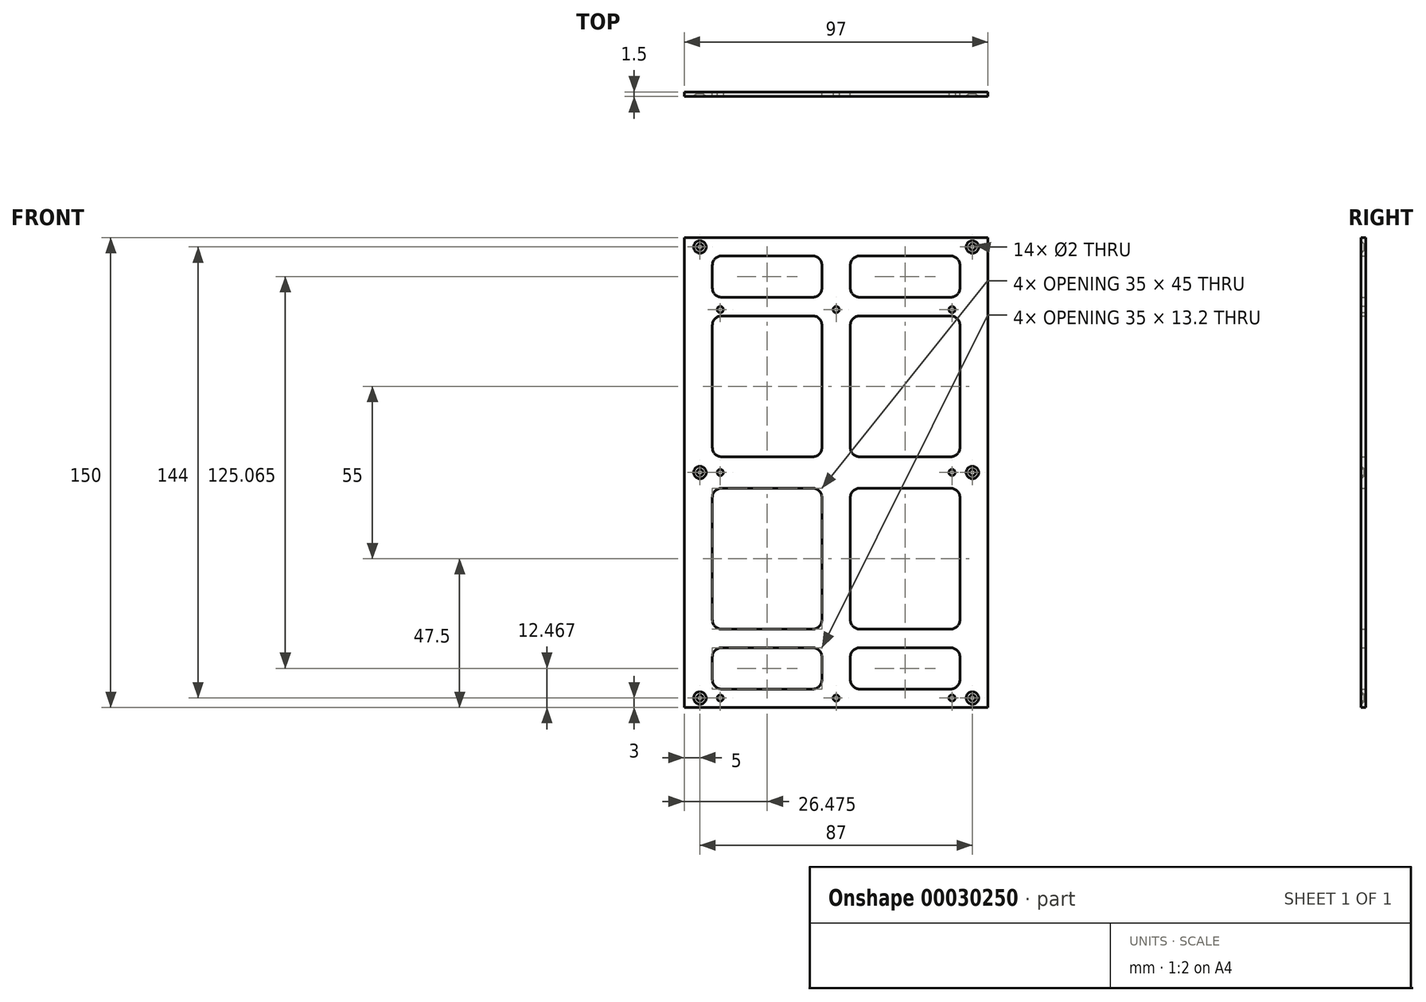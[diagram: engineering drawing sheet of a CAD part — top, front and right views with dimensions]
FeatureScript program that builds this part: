
annotation { "Feature Type Name" : "Feature", "Feature Type Description" : "" }
export const myFeature = defineFeature(function(context is Context, id is Id, definition is map)
    precondition{}
    {
        {
            var Q0;
            Q0=qCreatedBy(makeId("Front.planeOp"),FACE);
            var sketch = newSketch(context, id + "F0", { "sketchPlane" : qUnion([Q0])});
            skLineSegment(sketch, "E0.rect.bottom", {"start": v(-48.5, 75) * mm, "end": v(48.5, 75) * mm});
            skLineSegment(sketch, "E0.rect.top", {"start": v(-48.5, -75) * mm, "end": v(48.5, -75) * mm});
            skLineSegment(sketch, "E0.rect.left", {"start": v(-48.5, 75) * mm, "end": v(-48.5, -75) * mm});
            skLineSegment(sketch, "E0.rect.right", {"start": v(48.5, 75) * mm, "end": v(48.5, -75) * mm});
            skPoint(sketch, "E0.rect.middle", {"position": v(0, 0) * mm});
            skLineSegment(sketch, "E1.rect.bottom", {"start": v(-7.52, 5) * mm, "end": v(-36.52, 5) * mm});
            skLineSegment(sketch, "E1.rect.top", {"start": v(-7.52, 50) * mm, "end": v(-36.52, 50) * mm});
            skLineSegment(sketch, "E1.rect.left", {"start": v(-4.52, 8) * mm, "end": v(-4.52, 47) * mm});
            skLineSegment(sketch, "E1.rect.right", {"start": v(-39.52, 8) * mm, "end": v(-39.52, 47) * mm});
            skPoint(sketch, "E1.rect.middle", {"position": v(-22.02, 27.5) * mm});
            skPoint(sketch, "E2", {"position": v(0, 75) * mm});
            skPoint(sketch, "E3", {"position": v(-24.25, 75) * mm});
            skPoint(sketch, "E4.MirrorP", {"position": v(-24.25, -75) * mm});
            skPoint(sketch, "E5.visualSharp", {"position": v(-4.52, 5) * mm});
            skArc(sketch, "E5.filletArc", {"start": v(-7.52, 5) * mm, "mid": v(-5.4, 5.88) * mm, "end": v(-4.52, 8) * mm});
            skPoint(sketch, "E6.visualSharp", {"position": v(-4.52, 50) * mm});
            skArc(sketch, "E6.filletArc", {"start": v(-4.52, 47) * mm, "mid": v(-5.4, 49.12) * mm, "end": v(-7.52, 50) * mm});
            skPoint(sketch, "E7.visualSharp", {"position": v(-39.52, 50) * mm});
            skArc(sketch, "E7.filletArc", {"start": v(-36.52, 50) * mm, "mid": v(-38.65, 49.12) * mm, "end": v(-39.52, 47) * mm});
            skPoint(sketch, "E8.visualSharp", {"position": v(-39.52, 5) * mm});
            skArc(sketch, "E8.filletArc", {"start": v(-39.52, 8) * mm, "mid": v(-38.65, 5.88) * mm, "end": v(-36.52, 5) * mm});
            skLineSegment(sketch, "E9.MirrorCS", {"start": v(4.52, 8) * mm, "end": v(4.52, 47) * mm});
            skArc(sketch, "E10.MirrorCS", {"start": v(4.52, 47) * mm, "mid": v(5.4, 49.12) * mm, "end": v(7.52, 50) * mm});
            skLineSegment(sketch, "E11.MirrorCS", {"start": v(7.52, 50) * mm, "end": v(36.52, 50) * mm});
            skPoint(sketch, "E12.MirrorP", {"position": v(39.52, 50) * mm});
            skArc(sketch, "E13.MirrorCS", {"start": v(36.52, 50) * mm, "mid": v(38.65, 49.12) * mm, "end": v(39.52, 47) * mm});
            skLineSegment(sketch, "E14.MirrorCS", {"start": v(39.52, 8) * mm, "end": v(39.52, 47) * mm});
            skPoint(sketch, "E15.MirrorP", {"position": v(39.52, 5) * mm});
            skLineSegment(sketch, "E16.MirrorCS", {"start": v(7.52, 5) * mm, "end": v(36.52, 5) * mm});
            skArc(sketch, "E17.MirrorCS", {"start": v(39.52, 8) * mm, "mid": v(38.65, 5.88) * mm, "end": v(36.52, 5) * mm});
            skPoint(sketch, "E18.MirrorP", {"position": v(4.52, 5) * mm});
            skArc(sketch, "E19.MirrorCS", {"start": v(7.52, 5) * mm, "mid": v(5.4, 5.88) * mm, "end": v(4.52, 8) * mm});
            skPoint(sketch, "E20.MirrorP", {"position": v(4.52, 50) * mm});
            skArc(sketch, "E21.MirrorCS", {"start": v(36.52, -50) * mm, "mid": v(38.65, -49.12) * mm, "end": v(39.52, -47) * mm});
            skArc(sketch, "E22.MirrorCS", {"start": v(39.52, -8) * mm, "mid": v(38.65, -5.88) * mm, "end": v(36.52, -5) * mm});
            skArc(sketch, "E23.MirrorCS", {"start": v(7.52, -5) * mm, "mid": v(5.4, -5.88) * mm, "end": v(4.52, -8) * mm});
            skArc(sketch, "E24.MirrorCS", {"start": v(4.52, -47) * mm, "mid": v(5.4, -49.12) * mm, "end": v(7.52, -50) * mm});
            skPoint(sketch, "E25.MirrorP", {"position": v(39.52, -50) * mm});
            skLineSegment(sketch, "E26.MirrorCS", {"start": v(39.52, -8) * mm, "end": v(39.52, -47) * mm});
            skPoint(sketch, "E27.MirrorP", {"position": v(39.52, -5) * mm});
            skLineSegment(sketch, "E28.MirrorCS", {"start": v(4.52, -8) * mm, "end": v(4.52, -47) * mm});
            skPoint(sketch, "E29.MirrorP", {"position": v(4.52, -50) * mm});
            skLineSegment(sketch, "E30.MirrorCS", {"start": v(7.52, -5) * mm, "end": v(36.52, -5) * mm});
            skLineSegment(sketch, "E31.MirrorCS", {"start": v(7.52, -50) * mm, "end": v(36.52, -50) * mm});
            skPoint(sketch, "E32.MirrorP", {"position": v(4.52, -5) * mm});
            skArc(sketch, "E33.MirrorCS", {"start": v(-7.52, -5) * mm, "mid": v(-5.4, -5.88) * mm, "end": v(-4.52, -8) * mm});
            skArc(sketch, "E34.MirrorCS", {"start": v(-4.52, -47) * mm, "mid": v(-5.4, -49.12) * mm, "end": v(-7.52, -50) * mm});
            skArc(sketch, "E35.MirrorCS", {"start": v(-39.52, -8) * mm, "mid": v(-38.65, -5.88) * mm, "end": v(-36.52, -5) * mm});
            skArc(sketch, "E36.MirrorCS", {"start": v(-36.52, -50) * mm, "mid": v(-38.65, -49.12) * mm, "end": v(-39.52, -47) * mm});
            skPoint(sketch, "E37.MirrorP", {"position": v(-22.02, -27.5) * mm});
            skPoint(sketch, "E38.MirrorP", {"position": v(-4.52, -5) * mm});
            skPoint(sketch, "E39.MirrorP", {"position": v(-39.52, -50) * mm});
            skLineSegment(sketch, "E40.MirrorCS", {"start": v(-7.52, -5) * mm, "end": v(-36.52, -5) * mm});
            skLineSegment(sketch, "E41.MirrorCS", {"start": v(-7.52, -50) * mm, "end": v(-36.52, -50) * mm});
            skPoint(sketch, "E42.MirrorP", {"position": v(-4.52, -50) * mm});
            skLineSegment(sketch, "E43.MirrorCS", {"start": v(-4.52, -8) * mm, "end": v(-4.52, -47) * mm});
            skLineSegment(sketch, "E44.MirrorCS", {"start": v(-39.52, -8) * mm, "end": v(-39.52, -47) * mm});
            skPoint(sketch, "E45.MirrorP", {"position": v(-39.52, -5) * mm});
            skLineSegment(sketch, "E46.bottom", {"start": v(-7.52, 55.93) * mm, "end": v(-36.52, 55.93) * mm});
            skLineSegment(sketch, "E46.top", {"start": v(-7.52, 69.13) * mm, "end": v(-36.52, 69.13) * mm});
            skLineSegment(sketch, "E46.left", {"start": v(-4.52, 58.93) * mm, "end": v(-4.52, 66.13) * mm});
            skLineSegment(sketch, "E46.right", {"start": v(-39.52, 58.93) * mm, "end": v(-39.52, 66.13) * mm});
            skPoint(sketch, "E47.visualSharp", {"position": v(-39.52, 69.13) * mm});
            skArc(sketch, "E47.filletArc", {"start": v(-36.52, 69.13) * mm, "mid": v(-38.65, 68.26) * mm, "end": v(-39.52, 66.13) * mm});
            skPoint(sketch, "E48.visualSharp", {"position": v(-4.52, 69.13) * mm});
            skArc(sketch, "E48.filletArc", {"start": v(-4.52, 66.13) * mm, "mid": v(-5.4, 68.26) * mm, "end": v(-7.52, 69.13) * mm});
            skPoint(sketch, "E49.visualSharp", {"position": v(-4.52, 55.93) * mm});
            skArc(sketch, "E49.filletArc", {"start": v(-7.52, 55.93) * mm, "mid": v(-5.4, 56.8) * mm, "end": v(-4.52, 58.93) * mm});
            skPoint(sketch, "E50.visualSharp", {"position": v(-39.52, 55.93) * mm});
            skArc(sketch, "E50.filletArc", {"start": v(-39.52, 58.93) * mm, "mid": v(-38.65, 56.8) * mm, "end": v(-36.52, 55.93) * mm});
            skArc(sketch, "E51.MirrorCS", {"start": v(36.52, 69.13) * mm, "mid": v(38.65, 68.26) * mm, "end": v(39.52, 66.13) * mm});
            skArc(sketch, "E52.MirrorCS", {"start": v(4.52, 66.13) * mm, "mid": v(5.4, 68.26) * mm, "end": v(7.52, 69.13) * mm});
            skArc(sketch, "E53.MirrorCS", {"start": v(39.52, 58.93) * mm, "mid": v(38.65, 56.8) * mm, "end": v(36.52, 55.93) * mm});
            skArc(sketch, "E54.MirrorCS", {"start": v(7.52, 55.93) * mm, "mid": v(5.4, 56.8) * mm, "end": v(4.52, 58.93) * mm});
            skPoint(sketch, "E55.MirrorP", {"position": v(39.52, 55.93) * mm});
            skPoint(sketch, "E56.MirrorP", {"position": v(39.52, 69.13) * mm});
            skLineSegment(sketch, "E57.MirrorCS", {"start": v(39.52, 58.93) * mm, "end": v(39.52, 66.13) * mm});
            skPoint(sketch, "E58.MirrorP", {"position": v(4.52, 69.13) * mm});
            skLineSegment(sketch, "E59.MirrorCS", {"start": v(7.52, 69.13) * mm, "end": v(36.52, 69.13) * mm});
            skLineSegment(sketch, "E60.MirrorCS", {"start": v(4.52, 58.93) * mm, "end": v(4.52, 66.13) * mm});
            skLineSegment(sketch, "E61.MirrorCS", {"start": v(7.52, 55.93) * mm, "end": v(36.52, 55.93) * mm});
            skPoint(sketch, "E62.MirrorP", {"position": v(4.52, 55.93) * mm});
            skArc(sketch, "E63.MirrorCS", {"start": v(-4.52, -66.13) * mm, "mid": v(-5.4, -68.26) * mm, "end": v(-7.52, -69.13) * mm});
            skArc(sketch, "E64.MirrorCS", {"start": v(-36.52, -69.13) * mm, "mid": v(-38.65, -68.26) * mm, "end": v(-39.52, -66.13) * mm});
            skArc(sketch, "E65.MirrorCS", {"start": v(-39.52, -58.93) * mm, "mid": v(-38.65, -56.8) * mm, "end": v(-36.52, -55.93) * mm});
            skArc(sketch, "E66.MirrorCS", {"start": v(-7.52, -55.93) * mm, "mid": v(-5.4, -56.8) * mm, "end": v(-4.52, -58.93) * mm});
            skPoint(sketch, "E67.MirrorP", {"position": v(-39.52, -69.13) * mm});
            skPoint(sketch, "E68.MirrorP", {"position": v(-4.52, -55.93) * mm});
            skPoint(sketch, "E69.MirrorP", {"position": v(-4.52, -69.13) * mm});
            skLineSegment(sketch, "E70.MirrorCS", {"start": v(-39.52, -58.93) * mm, "end": v(-39.52, -66.13) * mm});
            skLineSegment(sketch, "E71.MirrorCS", {"start": v(-7.52, -69.13) * mm, "end": v(-36.52, -69.13) * mm});
            skPoint(sketch, "E72.MirrorP", {"position": v(-39.52, -55.93) * mm});
            skLineSegment(sketch, "E73.MirrorCS", {"start": v(-4.52, -58.93) * mm, "end": v(-4.52, -66.13) * mm});
            skLineSegment(sketch, "E74.MirrorCS", {"start": v(-7.52, -55.93) * mm, "end": v(-36.52, -55.93) * mm});
            skArc(sketch, "E75.MirrorCS", {"start": v(7.52, -55.93) * mm, "mid": v(5.4, -56.8) * mm, "end": v(4.52, -58.93) * mm});
            skArc(sketch, "E76.MirrorCS", {"start": v(39.52, -58.93) * mm, "mid": v(38.65, -56.8) * mm, "end": v(36.52, -55.93) * mm});
            skArc(sketch, "E77.MirrorCS", {"start": v(4.52, -66.13) * mm, "mid": v(5.4, -68.26) * mm, "end": v(7.52, -69.13) * mm});
            skArc(sketch, "E78.MirrorCS", {"start": v(36.52, -69.13) * mm, "mid": v(38.65, -68.26) * mm, "end": v(39.52, -66.13) * mm});
            skPoint(sketch, "E79.MirrorP", {"position": v(39.52, -69.13) * mm});
            skLineSegment(sketch, "E80.MirrorCS", {"start": v(7.52, -55.93) * mm, "end": v(36.52, -55.93) * mm});
            skPoint(sketch, "E81.MirrorP", {"position": v(4.52, -69.13) * mm});
            skLineSegment(sketch, "E82.MirrorCS", {"start": v(4.52, -58.93) * mm, "end": v(4.52, -66.13) * mm});
            skLineSegment(sketch, "E83.MirrorCS", {"start": v(39.52, -58.93) * mm, "end": v(39.52, -66.13) * mm});
            skLineSegment(sketch, "E84.MirrorCS", {"start": v(7.52, -69.13) * mm, "end": v(36.52, -69.13) * mm});
            skPoint(sketch, "E85.MirrorP", {"position": v(39.52, -55.93) * mm});
            skPoint(sketch, "E86.MirrorP", {"position": v(4.52, -55.93) * mm});
            skSolve(sketch);
        }
        {
            var Q0;
            Q0=makeQuery(id+"F0.imprint","IMPRINT",FACE,{"disambiguationData":[TD([[makeQuery(id+"F0.imprint","IMPRINT",EDGE,{"derivedFrom":sQuery(id+"F0.wireOp",EDGE,"E0.rect.bottom")}),-1.0]])]});
            extrude(context, id + "F1", {"entities" : qUnion([Q0]), "depth" : 1.5 * mm});
        }
        {
            var Q0;
            Q0=makeQuery(id+"F1.opExtrude","CAP_FACE",FACE,{"disambiguationData":[OSD([sQuery(id+"F0.wireOp",EDGE,"E0.rect.bottom"),sQuery(id+"F0.wireOp",EDGE,"E0.rect.top"),sQuery(id+"F0.wireOp",EDGE,"E0.rect.left"),sQuery(id+"F0.wireOp",EDGE,"E0.rect.right"),sQuery(id+"F0.wireOp",EDGE,"E1.rect.bottom"),sQuery(id+"F0.wireOp",EDGE,"E1.rect.top"),sQuery(id+"F0.wireOp",EDGE,"E1.rect.left"),sQuery(id+"F0.wireOp",EDGE,"E1.rect.right"),sQuery(id+"F0.wireOp",EDGE,"E5.filletArc"),sQuery(id+"F0.wireOp",EDGE,"E6.filletArc"),sQuery(id+"F0.wireOp",EDGE,"E7.filletArc"),sQuery(id+"F0.wireOp",EDGE,"E8.filletArc"),sQuery(id+"F0.wireOp",EDGE,"E9.MirrorCS"),sQuery(id+"F0.wireOp",EDGE,"E10.MirrorCS"),sQuery(id+"F0.wireOp",EDGE,"E11.MirrorCS"),sQuery(id+"F0.wireOp",EDGE,"E13.MirrorCS"),sQuery(id+"F0.wireOp",EDGE,"E14.MirrorCS"),sQuery(id+"F0.wireOp",EDGE,"E16.MirrorCS"),sQuery(id+"F0.wireOp",EDGE,"E17.MirrorCS"),sQuery(id+"F0.wireOp",EDGE,"E19.MirrorCS"),sQuery(id+"F0.wireOp",EDGE,"E21.MirrorCS"),sQuery(id+"F0.wireOp",EDGE,"E22.MirrorCS"),sQuery(id+"F0.wireOp",EDGE,"E23.MirrorCS"),sQuery(id+"F0.wireOp",EDGE,"E24.MirrorCS"),sQuery(id+"F0.wireOp",EDGE,"E26.MirrorCS"),sQuery(id+"F0.wireOp",EDGE,"E28.MirrorCS"),sQuery(id+"F0.wireOp",EDGE,"E30.MirrorCS"),sQuery(id+"F0.wireOp",EDGE,"E31.MirrorCS"),sQuery(id+"F0.wireOp",EDGE,"E33.MirrorCS"),sQuery(id+"F0.wireOp",EDGE,"E34.MirrorCS"),sQuery(id+"F0.wireOp",EDGE,"E35.MirrorCS"),sQuery(id+"F0.wireOp",EDGE,"E36.MirrorCS"),sQuery(id+"F0.wireOp",EDGE,"E40.MirrorCS"),sQuery(id+"F0.wireOp",EDGE,"E41.MirrorCS"),sQuery(id+"F0.wireOp",EDGE,"E43.MirrorCS"),sQuery(id+"F0.wireOp",EDGE,"E44.MirrorCS"),sQuery(id+"F0.wireOp",EDGE,"deea28ce-c4f6-4fc3-8f0f-82602a925565.rect.bottom"),sQuery(id+"F0.wireOp",EDGE,"deea28ce-c4f6-4fc3-8f0f-82602a925565.rect.top"),sQuery(id+"F0.wireOp",EDGE,"deea28ce-c4f6-4fc3-8f0f-82602a925565.rect.left"),sQuery(id+"F0.wireOp",EDGE,"deea28ce-c4f6-4fc3-8f0f-82602a925565.rect.right"),sQuery(id+"F0.wireOp",EDGE,"92293470-82ba-44ad-9286-e8a1911384cd.filletArc"),sQuery(id+"F0.wireOp",EDGE,"f783d059-47c1-4597-a3b5-ce5ed20d1783.filletArc"),sQuery(id+"F0.wireOp",EDGE,"7d8a2005-66fb-4448-9a0b-17e6f11710ed.filletArc"),sQuery(id+"F0.wireOp",EDGE,"bd1f88c4-01d0-4c1f-b818-689555ed0d3d.filletArc"),sQuery(id+"F0.wireOp",EDGE,"3de75153-5ae1-45d4-89d9-6fcf70203f930.MirrorCS"),sQuery(id+"F0.wireOp",EDGE,"3de75153-5ae1-45d4-89d9-6fcf70203f931.MirrorCS"),sQuery(id+"F0.wireOp",EDGE,"3de75153-5ae1-45d4-89d9-6fcf70203f932.MirrorCS"),sQuery(id+"F0.wireOp",EDGE,"3de75153-5ae1-45d4-89d9-6fcf70203f933.MirrorCS"),sQuery(id+"F0.wireOp",EDGE,"3de75153-5ae1-45d4-89d9-6fcf70203f937.MirrorCS"),sQuery(id+"F0.wireOp",EDGE,"3de75153-5ae1-45d4-89d9-6fcf70203f939.MirrorCS"),sQuery(id+"F0.wireOp",EDGE,"3de75153-5ae1-45d4-89d9-6fcf70203f9311.MirrorCS"),sQuery(id+"F0.wireOp",EDGE,"3de75153-5ae1-45d4-89d9-6fcf70203f9312.MirrorCS")])],"isStart":false});
            var sketch = newSketch(context, id + "F2", { "sketchPlane" : qUnion([Q0])});
            skPoint(sketch, "E87", {"position": v(-43.5, -72) * mm});
            skPoint(sketch, "E88.MirrorP", {"position": v(43.5, -72) * mm});
            skPoint(sketch, "E89.MirrorP", {"position": v(-43.5, 72) * mm});
            skPoint(sketch, "E90.MirrorP", {"position": v(43.5, 72) * mm});
            skPoint(sketch, "E91", {"position": v(-43.5, 0) * mm});
            skPoint(sketch, "E92.MirrorP", {"position": v(43.5, 0) * mm});
            skSolve(sketch);
        }
        {
            var Q0;
            Q0=sQuery(id+"F2.wireOp",VERTEX,"E87");
            var Q1;
            Q1=sQuery(id+"F2.wireOp",VERTEX,"E88.MirrorP");
            var Q2;
            Q2=sQuery(id+"F2.wireOp",VERTEX,"E90.MirrorP");
            var Q3;
            Q3=sQuery(id+"F2.wireOp",VERTEX,"E89.MirrorP");
            var Q4;
            Q4=sQuery(id+"F2.wireOp",VERTEX,"f692f96d-b3ef-4b25-bd05-95c4abe1053b");
            var Q5;
            Q5=sQuery(id+"F2.wireOp",VERTEX,"6fb1c37c-decf-44f5-8bba-7a2e60b1c09a");
            var Q6;
            Q6=sQuery(id+"F2.wireOp",VERTEX,"e5432b45-bd6c-42e0-96c4-d4a1cdefc3be");
            var Q7;
            Q7=sQuery(id+"F2.wireOp",VERTEX,"cf76a1ca-a373-4096-b586-4708a9325641");
            var Q8;
            Q8=sQuery(id+"F2.wireOp",VERTEX,"19e9ac87-c4db-4f84-8793-d0dcfe6b89480.MirrorP");
            var Q9;
            Q9=sQuery(id+"F2.wireOp",VERTEX,"cf40c92d-3cb4-4fd1-9011-2b1b11cf86800.MirrorP");
            var Q10;
            Q10=sQuery(id+"F2.wireOp",VERTEX,"dbe2afd2-cc13-4726-9d4e-a7426feb8f1a0.MirrorP");
            var Q11;
            Q11=sQuery(id+"F2.wireOp",VERTEX,"da7565b5-0760-4871-9ab9-0602c46f39720.MirrorP");
            var Q12;
            Q12=sQuery(id+"F2.wireOp",VERTEX,"17fecccd-3962-452f-9978-7328e825eee30.MirrorP");
            var Q13;
            Q13=sQuery(id+"F2.wireOp",VERTEX,"4bd07c42-14cb-4c0a-9484-79320a5c3db60.MirrorP");
            var Q14;
            Q14=sQuery(id+"F2.wireOp",VERTEX,"4bebc43e-6cee-4dba-a944-25e79cf908630.MirrorP");
            var Q15;
            Q15=sQuery(id+"F2.wireOp",VERTEX,"e56d2771-9223-44ee-8796-3a5c91e851be0.MirrorP");
            var Q16;
            Q16=sQuery(id+"F2.wireOp",VERTEX,"fc323023-5ca8-47af-bc60-2d4e8e6fe2a30.MirrorP");
            var Q17;
            Q17=sQuery(id+"F2.wireOp",VERTEX,"0839c29d-2d7f-409f-b01c-e3268e62f07b0.MirrorP");
            var Q18;
            Q18=sQuery(id+"F2.wireOp",VERTEX,"a23aa490-2248-47f4-872f-093390e742580.MirrorP");
            var Q19;
            Q19=sQuery(id+"F2.wireOp",VERTEX,"f29489ae-a8f8-488d-b8ee-71de4e1048c30.MirrorP");
            var Q20;
            Q20=sQuery(id+"F2.wireOp",VERTEX,"E91");
            var Q21;
            Q21=sQuery(id+"F2.wireOp",VERTEX,"E92.MirrorP");
            var Q22;
            Q22=makeQuery(id+"F1.opExtrude","SWEPT_BODY",BODY,{"disambiguationData":[OSD([sQuery(id+"F0.wireOp",EDGE,"E0.rect.bottom"),sQuery(id+"F0.wireOp",EDGE,"E0.rect.top"),sQuery(id+"F0.wireOp",EDGE,"E0.rect.left"),sQuery(id+"F0.wireOp",EDGE,"E0.rect.right"),sQuery(id+"F0.wireOp",EDGE,"E1.rect.bottom"),sQuery(id+"F0.wireOp",EDGE,"E1.rect.top"),sQuery(id+"F0.wireOp",EDGE,"E1.rect.left"),sQuery(id+"F0.wireOp",EDGE,"E1.rect.right"),sQuery(id+"F0.wireOp",EDGE,"E5.filletArc"),sQuery(id+"F0.wireOp",EDGE,"E6.filletArc"),sQuery(id+"F0.wireOp",EDGE,"E7.filletArc"),sQuery(id+"F0.wireOp",EDGE,"E8.filletArc"),sQuery(id+"F0.wireOp",EDGE,"E9.MirrorCS"),sQuery(id+"F0.wireOp",EDGE,"E10.MirrorCS"),sQuery(id+"F0.wireOp",EDGE,"E11.MirrorCS"),sQuery(id+"F0.wireOp",EDGE,"E13.MirrorCS"),sQuery(id+"F0.wireOp",EDGE,"E14.MirrorCS"),sQuery(id+"F0.wireOp",EDGE,"E16.MirrorCS"),sQuery(id+"F0.wireOp",EDGE,"E17.MirrorCS"),sQuery(id+"F0.wireOp",EDGE,"E19.MirrorCS"),sQuery(id+"F0.wireOp",EDGE,"E21.MirrorCS"),sQuery(id+"F0.wireOp",EDGE,"E22.MirrorCS"),sQuery(id+"F0.wireOp",EDGE,"E23.MirrorCS"),sQuery(id+"F0.wireOp",EDGE,"E24.MirrorCS"),sQuery(id+"F0.wireOp",EDGE,"E26.MirrorCS"),sQuery(id+"F0.wireOp",EDGE,"E28.MirrorCS"),sQuery(id+"F0.wireOp",EDGE,"E30.MirrorCS"),sQuery(id+"F0.wireOp",EDGE,"E31.MirrorCS"),sQuery(id+"F0.wireOp",EDGE,"E33.MirrorCS"),sQuery(id+"F0.wireOp",EDGE,"E34.MirrorCS"),sQuery(id+"F0.wireOp",EDGE,"E35.MirrorCS"),sQuery(id+"F0.wireOp",EDGE,"E36.MirrorCS"),sQuery(id+"F0.wireOp",EDGE,"E40.MirrorCS"),sQuery(id+"F0.wireOp",EDGE,"E41.MirrorCS"),sQuery(id+"F0.wireOp",EDGE,"E43.MirrorCS"),sQuery(id+"F0.wireOp",EDGE,"E44.MirrorCS"),sQuery(id+"F0.wireOp",EDGE,"deea28ce-c4f6-4fc3-8f0f-82602a925565.rect.bottom"),sQuery(id+"F0.wireOp",EDGE,"deea28ce-c4f6-4fc3-8f0f-82602a925565.rect.top"),sQuery(id+"F0.wireOp",EDGE,"deea28ce-c4f6-4fc3-8f0f-82602a925565.rect.left"),sQuery(id+"F0.wireOp",EDGE,"deea28ce-c4f6-4fc3-8f0f-82602a925565.rect.right"),sQuery(id+"F0.wireOp",EDGE,"92293470-82ba-44ad-9286-e8a1911384cd.filletArc"),sQuery(id+"F0.wireOp",EDGE,"f783d059-47c1-4597-a3b5-ce5ed20d1783.filletArc"),sQuery(id+"F0.wireOp",EDGE,"7d8a2005-66fb-4448-9a0b-17e6f11710ed.filletArc"),sQuery(id+"F0.wireOp",EDGE,"bd1f88c4-01d0-4c1f-b818-689555ed0d3d.filletArc"),sQuery(id+"F0.wireOp",EDGE,"3de75153-5ae1-45d4-89d9-6fcf70203f930.MirrorCS"),sQuery(id+"F0.wireOp",EDGE,"3de75153-5ae1-45d4-89d9-6fcf70203f931.MirrorCS"),sQuery(id+"F0.wireOp",EDGE,"3de75153-5ae1-45d4-89d9-6fcf70203f932.MirrorCS"),sQuery(id+"F0.wireOp",EDGE,"3de75153-5ae1-45d4-89d9-6fcf70203f933.MirrorCS"),sQuery(id+"F0.wireOp",EDGE,"3de75153-5ae1-45d4-89d9-6fcf70203f937.MirrorCS"),sQuery(id+"F0.wireOp",EDGE,"3de75153-5ae1-45d4-89d9-6fcf70203f939.MirrorCS"),sQuery(id+"F0.wireOp",EDGE,"3de75153-5ae1-45d4-89d9-6fcf70203f9311.MirrorCS"),sQuery(id+"F0.wireOp",EDGE,"3de75153-5ae1-45d4-89d9-6fcf70203f9312.MirrorCS")])]});
            hole(context, id + "F3", {"style" : HoleStyle.C_SINK, "holeDiameter" : 2 * mm, "cSinkDiameter" : 4 * mm, "endStyle" : HoleEndStyle.THROUGH, "locations" : qUnion([Q0, Q1, Q2, Q3, Q4, Q5, Q6, Q7, Q8, Q9, Q10, Q11, Q12, Q13, Q14, Q15, Q16, Q17, Q18, Q19, Q20, Q21]), "scope" : qUnion([Q22]), "cSinkAngle" : 90 * degree, "isTappedThrough" : true});
        }
        {
            var Q0;
            Q0=makeQuery(id+"F1.opExtrude","CAP_FACE",FACE,{"disambiguationData":[OSD([sQuery(id+"F0.wireOp",EDGE,"E0.rect.bottom"),sQuery(id+"F0.wireOp",EDGE,"E0.rect.top"),sQuery(id+"F0.wireOp",EDGE,"E0.rect.left"),sQuery(id+"F0.wireOp",EDGE,"E0.rect.right"),sQuery(id+"F0.wireOp",EDGE,"E1.rect.bottom"),sQuery(id+"F0.wireOp",EDGE,"E1.rect.top"),sQuery(id+"F0.wireOp",EDGE,"E1.rect.left"),sQuery(id+"F0.wireOp",EDGE,"E1.rect.right"),sQuery(id+"F0.wireOp",EDGE,"E5.filletArc"),sQuery(id+"F0.wireOp",EDGE,"E6.filletArc"),sQuery(id+"F0.wireOp",EDGE,"E7.filletArc"),sQuery(id+"F0.wireOp",EDGE,"E8.filletArc"),sQuery(id+"F0.wireOp",EDGE,"E9.MirrorCS"),sQuery(id+"F0.wireOp",EDGE,"E10.MirrorCS"),sQuery(id+"F0.wireOp",EDGE,"E11.MirrorCS"),sQuery(id+"F0.wireOp",EDGE,"E13.MirrorCS"),sQuery(id+"F0.wireOp",EDGE,"E14.MirrorCS"),sQuery(id+"F0.wireOp",EDGE,"E16.MirrorCS"),sQuery(id+"F0.wireOp",EDGE,"E17.MirrorCS"),sQuery(id+"F0.wireOp",EDGE,"E19.MirrorCS"),sQuery(id+"F0.wireOp",EDGE,"E21.MirrorCS"),sQuery(id+"F0.wireOp",EDGE,"E22.MirrorCS"),sQuery(id+"F0.wireOp",EDGE,"E23.MirrorCS"),sQuery(id+"F0.wireOp",EDGE,"E24.MirrorCS"),sQuery(id+"F0.wireOp",EDGE,"E26.MirrorCS"),sQuery(id+"F0.wireOp",EDGE,"E28.MirrorCS"),sQuery(id+"F0.wireOp",EDGE,"E30.MirrorCS"),sQuery(id+"F0.wireOp",EDGE,"E31.MirrorCS"),sQuery(id+"F0.wireOp",EDGE,"E33.MirrorCS"),sQuery(id+"F0.wireOp",EDGE,"E34.MirrorCS"),sQuery(id+"F0.wireOp",EDGE,"E35.MirrorCS"),sQuery(id+"F0.wireOp",EDGE,"E36.MirrorCS"),sQuery(id+"F0.wireOp",EDGE,"E40.MirrorCS"),sQuery(id+"F0.wireOp",EDGE,"E41.MirrorCS"),sQuery(id+"F0.wireOp",EDGE,"E43.MirrorCS"),sQuery(id+"F0.wireOp",EDGE,"E44.MirrorCS"),sQuery(id+"F0.wireOp",EDGE,"88a51af2-b307-4e3c-8326-7cdc2dc0827f")])],"isStart":false});
            var sketch = newSketch(context, id + "F4", { "sketchPlane" : qUnion([Q0])});
            skCircle(sketch, "E93", {"center": v(-37, -72) * mm, "radius": 1 * mm});
            skCircle(sketch, "E94.0.1.0", {"center": v(-37, 52) * mm, "radius": 1 * mm});
            skCircle(sketch, "E94.1.0.0", {"center": v(0, -72) * mm, "radius": 1 * mm});
            skCircle(sketch, "E94.1.1.0", {"center": v(0, 52) * mm, "radius": 1 * mm});
            skCircle(sketch, "E94.2.0.0", {"center": v(37, -72) * mm, "radius": 1 * mm});
            skCircle(sketch, "E94.2.1.0", {"center": v(37, 52) * mm, "radius": 1 * mm});
            skLineSegment(sketch, "E94.direction1", {"start": v(-37, -72) * mm, "end": v(0, -72) * mm, "construction": true});
            skLineSegment(sketch, "E94.direction2", {"start": v(-37, -72) * mm, "end": v(-37, 52) * mm, "construction": true});
            skPoint(sketch, "E95", {"position": v(-37, 0) * mm});
            skPoint(sketch, "E96.MirrorP", {"position": v(37, 0) * mm});
            skSolve(sketch);
        }
        {
            var Q0;
            Q0=sQuery(id+"F4.wireOp",VERTEX,"E93.center");
            var Q1;
            Q1=sQuery(id+"F4.wireOp",VERTEX,"E94.1.0.0.center");
            var Q2;
            Q2=sQuery(id+"F4.wireOp",VERTEX,"E94.2.0.0.center");
            var Q3;
            Q3=sQuery(id+"F4.wireOp",VERTEX,"E94.1.1.0.center");
            var Q4;
            Q4=sQuery(id+"F4.wireOp",VERTEX,"E94.1.2.0.center");
            var Q5;
            Q5=sQuery(id+"F4.wireOp",VERTEX,"E94.0.1.0.center");
            var Q6;
            Q6=sQuery(id+"F4.wireOp",VERTEX,"E94.2.1.0.center");
            var Q7;
            Q7=sQuery(id+"F4.wireOp",VERTEX,"E95");
            var Q8;
            Q8=sQuery(id+"F4.wireOp",VERTEX,"E96.MirrorP");
            var Q9;
            Q9=makeQuery(id+"F1.opExtrude","SWEPT_BODY",BODY,{"disambiguationData":[OSD([sQuery(id+"F0.wireOp",EDGE,"E0.rect.bottom"),sQuery(id+"F0.wireOp",EDGE,"E0.rect.top"),sQuery(id+"F0.wireOp",EDGE,"E0.rect.left"),sQuery(id+"F0.wireOp",EDGE,"E0.rect.right"),sQuery(id+"F0.wireOp",EDGE,"E1.rect.bottom"),sQuery(id+"F0.wireOp",EDGE,"E1.rect.top"),sQuery(id+"F0.wireOp",EDGE,"E1.rect.left"),sQuery(id+"F0.wireOp",EDGE,"E1.rect.right"),sQuery(id+"F0.wireOp",EDGE,"E5.filletArc"),sQuery(id+"F0.wireOp",EDGE,"E6.filletArc"),sQuery(id+"F0.wireOp",EDGE,"E7.filletArc"),sQuery(id+"F0.wireOp",EDGE,"E8.filletArc"),sQuery(id+"F0.wireOp",EDGE,"E9.MirrorCS"),sQuery(id+"F0.wireOp",EDGE,"E10.MirrorCS"),sQuery(id+"F0.wireOp",EDGE,"E11.MirrorCS"),sQuery(id+"F0.wireOp",EDGE,"E13.MirrorCS"),sQuery(id+"F0.wireOp",EDGE,"E14.MirrorCS"),sQuery(id+"F0.wireOp",EDGE,"E16.MirrorCS"),sQuery(id+"F0.wireOp",EDGE,"E17.MirrorCS"),sQuery(id+"F0.wireOp",EDGE,"E19.MirrorCS"),sQuery(id+"F0.wireOp",EDGE,"E21.MirrorCS"),sQuery(id+"F0.wireOp",EDGE,"E22.MirrorCS"),sQuery(id+"F0.wireOp",EDGE,"E23.MirrorCS"),sQuery(id+"F0.wireOp",EDGE,"E24.MirrorCS"),sQuery(id+"F0.wireOp",EDGE,"E26.MirrorCS"),sQuery(id+"F0.wireOp",EDGE,"E28.MirrorCS"),sQuery(id+"F0.wireOp",EDGE,"E30.MirrorCS"),sQuery(id+"F0.wireOp",EDGE,"E31.MirrorCS"),sQuery(id+"F0.wireOp",EDGE,"E33.MirrorCS"),sQuery(id+"F0.wireOp",EDGE,"E34.MirrorCS"),sQuery(id+"F0.wireOp",EDGE,"E35.MirrorCS"),sQuery(id+"F0.wireOp",EDGE,"E36.MirrorCS"),sQuery(id+"F0.wireOp",EDGE,"E40.MirrorCS"),sQuery(id+"F0.wireOp",EDGE,"E41.MirrorCS"),sQuery(id+"F0.wireOp",EDGE,"E43.MirrorCS"),sQuery(id+"F0.wireOp",EDGE,"E44.MirrorCS"),sQuery(id+"F0.wireOp",EDGE,"88a51af2-b307-4e3c-8326-7cdc2dc0827f")])]});
            hole(context, id + "F5", {"style" : HoleStyle.SIMPLE, "endStyle" : HoleEndStyle.THROUGH, "holeDiameter" : 2 * mm, "locations" : qUnion([Q0, Q1, Q2, Q3, Q4, Q5, Q6, Q7, Q8]), "scope" : qUnion([Q9]), "isTappedThrough" : true});
        }
    });
